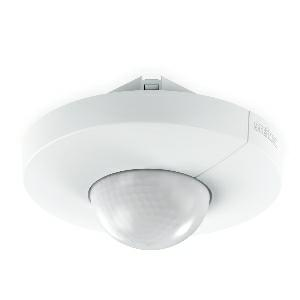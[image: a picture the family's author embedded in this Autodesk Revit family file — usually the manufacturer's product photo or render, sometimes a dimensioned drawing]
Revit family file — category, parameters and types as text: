
# Revit family: is_345_033873
name_source: partatom
category: Elektroinstallationen
revit_build: Autodesk Revit 2016 (Build: 20190508_0715(x64)
units: mm (PartAtom-declared; Revit-internal decimal feet)

## family parameters
Basisbauteil = Fläche
Beim Laden mit Abzugskörper schneiden = Nein
Bemaßung runder Anschluss = Durchmesser verwenden
Beschriftungsausrichtung beibehalten = Nein
Gemeinsam genutzt = Nein
Raumberechnungspunkt = Nein
Teiletyp = Normal

## types (1)
- IS 345
    Apparent Load = 0 VA
    Beschreibung = Type: Motion detectors; Dimensions (Ø x H): 124 x 78 mm; Mains power supply: 220 – 240 V / 50 – 60 Hz; Sensor Technology: passive infrared; Application, place: Indoors; Application, room: corridor / aisle, multi-storey / underground car park, Indoors; Installation site: ceiling; Installation: Concealed wiring; Switching zones: 280 switching zones; Electronic scalability: No; Mechanical scalability: No; Mounting height: 2,50 – 5,00 m; Optimum mounting height: 2,8 m; Detection angle: 360 °; Angle of aperture: 45 °; Sneak-by guard: Yes; Capability of masking out individual segments: Yes; Reach, radial: 12 x 6 m (72 m²); Reach, tangential: 23 x 6 m (138 m²); Twilight setting TEACH: Yes; Twilight setting: 2 – 1000 lx; Time setting: 5 sec – 15 min; Control output, Dali: Broadcast 1x30 electronic ballasts; Constant-lighting control: Yes; Basic light level function: Yes; Basic light level function in per cent: 10 – 50 %; Basic light level function time: 1-30 min, all night; Basic light level function percentage, from: 10 %; Basic light level function percentage, up to: 50 %; Functions: Normal / test mode, Manual ON / ON-OFF, Constant-lighting control ON-OFF; Settings via: Remote control, Potentiometers, Smart Remote; With remote control: No; Interconnection: Yes; IP-rating: IP20; Material: Plastic; Ambient temperature: -20 – 50 °C; Colour: white; Colour, RAL: 9003; Manufacturer's Warranty: 5 years; Version: DALI-2 Application Controller - concealed, rd.; PU1, EAN: 4007841033873
    Height = 0 mm  [stored 0 ft]
    Hersteller = Steinel
    Length = 124 mm  [stored 0.406824 ft]
    Maximum range = 11.589 m
    ModVariant = Nein
    Modell = 033873
    Mounting Place = Ceiling
    Mounting Type = Recessed
    Number of Poles = 1
    OnlyDefault = Ja
    Power Factor = 1
    Product Name = IS 345
    Product group = Presence detector
    ProductGroupID = 4
    Protection Class = Protection class
    Protection Degree = IP 20
    RlxData = <blob elided: 156829 chars, md5=d936d004>
    Sensor characteristics = Stretched
    Sensor type = Passive (infrared)
    SensorDataFile = <blob elided: 5885 chars, md5=98bccc25>
    Type of entry = Motion
    Typenbild = produkt1_033873.jpg
    Typenkommentare = Product without accessories
    URL = http://relux.com
    VarID = ---
    Voltage = 0 V
    Vorgabe-Ansicht = 1800 mm
    Weight = 0.00 kg
    Width = 0 mm  [stored 0 ft]

note: [stored X ft] marks values corroborated as IEEE doubles in the binary element streams (Revit-internal decimal feet)

## geometry (parser evidence)
native form markers: Blend x4, Sweep x19
no freeform markers — native parametric forms only
